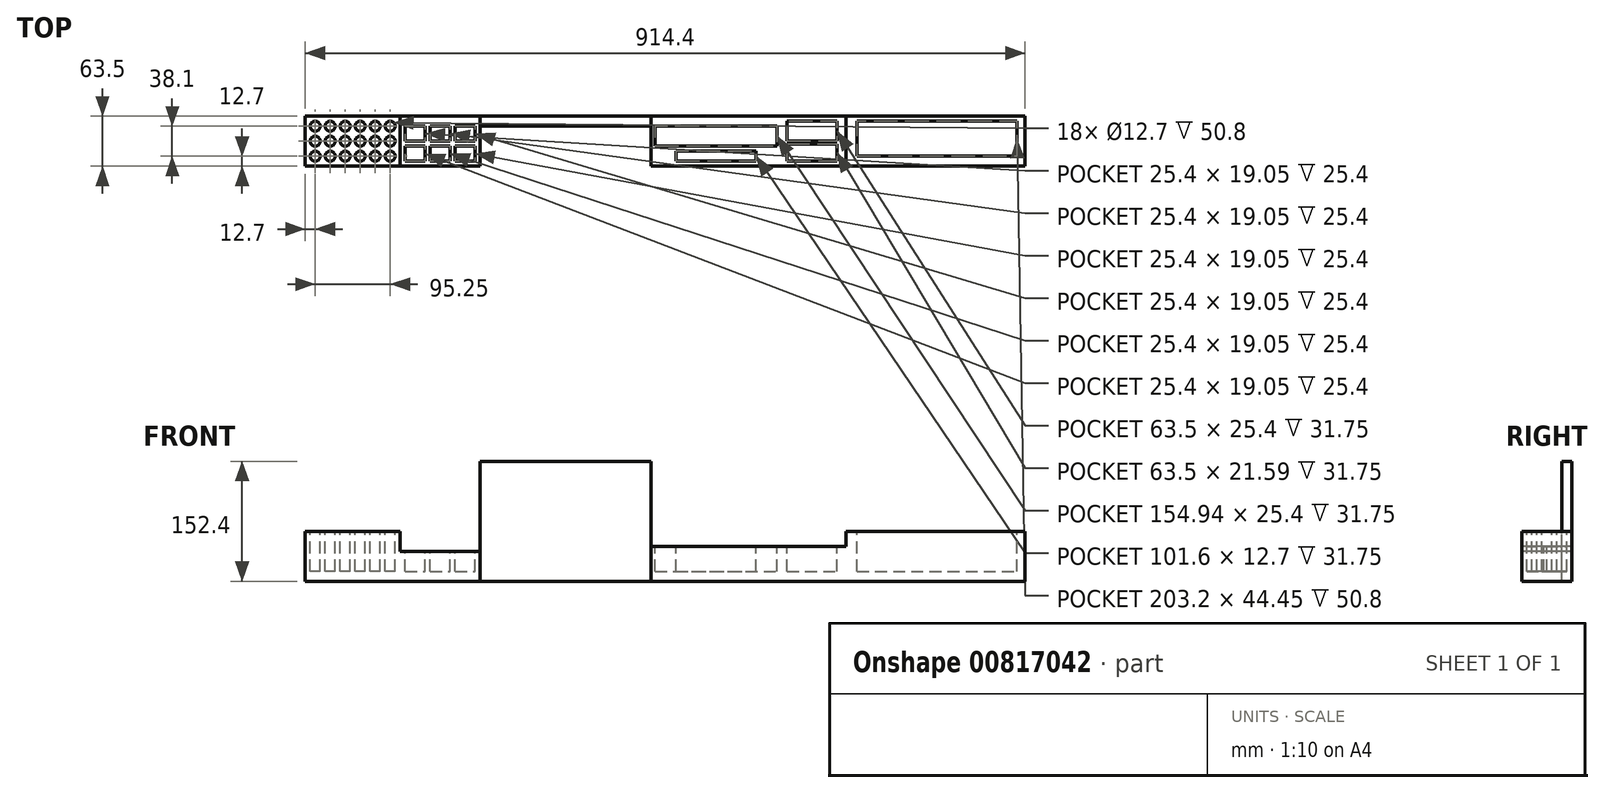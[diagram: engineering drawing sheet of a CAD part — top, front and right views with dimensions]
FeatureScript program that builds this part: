
annotation { "Feature Type Name" : "Feature", "Feature Type Description" : "" }
export const myFeature = defineFeature(function(context is Context, id is Id, definition is map)
    precondition{}
    {
        {
            var Q0;
            Q0=qCreatedBy(makeId("Front.planeOp"),FACE);
            var sketch = newSketch(context, id + "F0", { "sketchPlane" : qUnion([Q0])});
            skLineSegment(sketch, "E0.bottom", {"start": v(457.2, 76.2) * mm, "end": v(-457.2, 76.2) * mm});
            skLineSegment(sketch, "E0.top", {"start": v(457.2, -76.2) * mm, "end": v(-457.2, -76.2) * mm});
            skLineSegment(sketch, "E0.left", {"start": v(457.2, 76.2) * mm, "end": v(457.2, -76.2) * mm});
            skLineSegment(sketch, "E0.right", {"start": v(-457.2, 76.2) * mm, "end": v(-457.2, -76.2) * mm});
            skPoint(sketch, "E0.middle", {"position": v(0, 0) * mm});
            skSolve(sketch);
        }
        {
            var Q0;
            Q0=makeQuery(id+"F0.imprint","IMPRINT",FACE,{"disambiguationData":[TD([[makeQuery(id+"F0.imprint","IMPRINT",EDGE,{"derivedFrom":sQuery(id+"F0.wireOp",EDGE,"E0.bottom")}),1.0]])]});
            extrude(context, id + "F1", {"entities" : qUnion([Q0]), "depth" : 63.5 * mm, "offsetDistance" : 25.4 * mm});
        }
        {
            var Q0;
            Q0=makeQuery(id+"F1.opExtrude","SWEPT_FACE",FACE,{"disambiguationData":[OSD([sQuery(id+"F0.wireOp",EDGE,"E0.bottom")])]});
            var sketch = newSketch(context, id + "F2", { "sketchPlane" : qUnion([Q0])});
            skCircle(sketch, "E1", {"center": v(-444.5, -12.7) * mm, "radius": 6.35 * mm});
            skCircle(sketch, "E2", {"center": v(-425.45, -12.7) * mm, "radius": 6.35 * mm});
            skCircle(sketch, "E3", {"center": v(-406.4, -12.7) * mm, "radius": 6.35 * mm});
            skCircle(sketch, "E4", {"center": v(-387.35, -12.7) * mm, "radius": 6.35 * mm});
            skCircle(sketch, "E5", {"center": v(-368.3, -12.7) * mm, "radius": 6.35 * mm});
            skCircle(sketch, "E6", {"center": v(-349.25, -12.7) * mm, "radius": 6.35 * mm});
            skCircle(sketch, "E7", {"center": v(-444.5, -31.75) * mm, "radius": 6.35 * mm});
            skCircle(sketch, "E8", {"center": v(-425.45, -31.75) * mm, "radius": 6.35 * mm});
            skCircle(sketch, "E9", {"center": v(-406.4, -31.75) * mm, "radius": 6.35 * mm});
            skCircle(sketch, "E10", {"center": v(-387.35, -31.75) * mm, "radius": 6.35 * mm});
            skCircle(sketch, "E11", {"center": v(-368.3, -31.75) * mm, "radius": 6.35 * mm});
            skCircle(sketch, "E12", {"center": v(-349.25, -31.75) * mm, "radius": 6.35 * mm});
            skCircle(sketch, "E13", {"center": v(-444.5, -50.8) * mm, "radius": 6.35 * mm});
            skCircle(sketch, "E14", {"center": v(-425.45, -50.8) * mm, "radius": 6.35 * mm});
            skCircle(sketch, "E15", {"center": v(-406.4, -50.8) * mm, "radius": 6.35 * mm});
            skCircle(sketch, "E16", {"center": v(-387.35, -50.8) * mm, "radius": 6.35 * mm});
            skCircle(sketch, "E17", {"center": v(-368.3, -50.8) * mm, "radius": 6.35 * mm});
            skCircle(sketch, "E18", {"center": v(-349.25, -50.8) * mm, "radius": 6.35 * mm});
            skLineSegment(sketch, "E19.bottom", {"start": v(-330.2, -57.15) * mm, "end": v(-304.8, -57.15) * mm});
            skLineSegment(sketch, "E19.top", {"start": v(-330.2, -38.1) * mm, "end": v(-304.8, -38.1) * mm});
            skLineSegment(sketch, "E19.left", {"start": v(-330.2, -57.15) * mm, "end": v(-330.2, -38.1) * mm});
            skLineSegment(sketch, "E19.right", {"start": v(-304.8, -57.15) * mm, "end": v(-304.8, -38.1) * mm});
            skLineSegment(sketch, "E20.bottom", {"start": v(-330.2, -31.75) * mm, "end": v(-304.8, -31.75) * mm});
            skLineSegment(sketch, "E20.top", {"start": v(-330.2, -12.7) * mm, "end": v(-304.8, -12.7) * mm});
            skLineSegment(sketch, "E20.left", {"start": v(-330.2, -31.75) * mm, "end": v(-330.2, -12.7) * mm});
            skLineSegment(sketch, "E20.right", {"start": v(-304.8, -31.75) * mm, "end": v(-304.8, -12.7) * mm});
            skLineSegment(sketch, "E21.bottom", {"start": v(-298.45, -31.75) * mm, "end": v(-273.05, -31.75) * mm});
            skLineSegment(sketch, "E21.top", {"start": v(-298.45, -12.7) * mm, "end": v(-273.05, -12.7) * mm});
            skLineSegment(sketch, "E21.left", {"start": v(-298.45, -31.75) * mm, "end": v(-298.45, -12.7) * mm});
            skLineSegment(sketch, "E21.right", {"start": v(-273.05, -31.75) * mm, "end": v(-273.05, -12.7) * mm});
            skLineSegment(sketch, "E22.bottom", {"start": v(-298.45, -57.15) * mm, "end": v(-273.05, -57.15) * mm});
            skLineSegment(sketch, "E22.top", {"start": v(-298.45, -38.1) * mm, "end": v(-273.05, -38.1) * mm});
            skLineSegment(sketch, "E22.left", {"start": v(-298.45, -57.15) * mm, "end": v(-298.45, -38.1) * mm});
            skLineSegment(sketch, "E22.right", {"start": v(-273.05, -57.15) * mm, "end": v(-273.05, -38.1) * mm});
            skLineSegment(sketch, "E23.bottom", {"start": v(-266.7, -31.75) * mm, "end": v(-241.3, -31.75) * mm});
            skLineSegment(sketch, "E23.top", {"start": v(-266.7, -12.7) * mm, "end": v(-241.3, -12.7) * mm});
            skLineSegment(sketch, "E23.left", {"start": v(-266.7, -31.75) * mm, "end": v(-266.7, -12.7) * mm});
            skLineSegment(sketch, "E23.right", {"start": v(-241.3, -31.75) * mm, "end": v(-241.3, -12.7) * mm});
            skLineSegment(sketch, "E24.bottom", {"start": v(-266.7, -57.15) * mm, "end": v(-241.3, -57.15) * mm});
            skLineSegment(sketch, "E24.top", {"start": v(-266.7, -38.1) * mm, "end": v(-241.3, -38.1) * mm});
            skLineSegment(sketch, "E24.left", {"start": v(-266.7, -57.15) * mm, "end": v(-266.7, -38.1) * mm});
            skLineSegment(sketch, "E24.right", {"start": v(-241.3, -57.15) * mm, "end": v(-241.3, -38.1) * mm});
            skLineSegment(sketch, "E25", {"start": v(-228.6, 0) * mm, "end": v(-228.6, -63.5) * mm, "construction": true});
            skLineSegment(sketch, "E26", {"start": v(-25.4, 0) * mm, "end": v(-25.4, -63.5) * mm, "construction": true});
            skLineSegment(sketch, "E27.bottom", {"start": v(-12.7, -12.7) * mm, "end": v(142.24, -12.7) * mm});
            skLineSegment(sketch, "E27.top", {"start": v(-12.7, -38.1) * mm, "end": v(142.24, -38.1) * mm});
            skLineSegment(sketch, "E27.left", {"start": v(-12.7, -12.7) * mm, "end": v(-12.7, -38.1) * mm});
            skLineSegment(sketch, "E27.right", {"start": v(142.24, -12.7) * mm, "end": v(142.24, -38.1) * mm});
            skLineSegment(sketch, "E28.bottom", {"start": v(13.97, -44.45) * mm, "end": v(115.57, -44.45) * mm});
            skLineSegment(sketch, "E28.top", {"start": v(13.97, -57.15) * mm, "end": v(115.57, -57.15) * mm});
            skLineSegment(sketch, "E28.left", {"start": v(13.97, -44.45) * mm, "end": v(13.97, -57.15) * mm});
            skLineSegment(sketch, "E28.right", {"start": v(115.57, -44.45) * mm, "end": v(115.57, -57.15) * mm});
            skLineSegment(sketch, "E29.bottom", {"start": v(154.94, -6.35) * mm, "end": v(218.44, -6.35) * mm});
            skLineSegment(sketch, "E29.top", {"start": v(154.94, -31.75) * mm, "end": v(218.44, -31.75) * mm});
            skLineSegment(sketch, "E29.left", {"start": v(154.94, -6.35) * mm, "end": v(154.94, -31.75) * mm});
            skLineSegment(sketch, "E29.right", {"start": v(218.44, -6.35) * mm, "end": v(218.44, -31.75) * mm});
            skLineSegment(sketch, "E30.bottom", {"start": v(243.84, -6.35) * mm, "end": v(447.04, -6.35) * mm});
            skLineSegment(sketch, "E30.top", {"start": v(243.84, -50.8) * mm, "end": v(447.04, -50.8) * mm});
            skLineSegment(sketch, "E30.left", {"start": v(243.84, -6.35) * mm, "end": v(243.84, -50.8) * mm});
            skLineSegment(sketch, "E30.right", {"start": v(447.04, -6.35) * mm, "end": v(447.04, -50.8) * mm});
            skLineSegment(sketch, "E31.bottom", {"start": v(154.94, -57.15) * mm, "end": v(218.44, -57.15) * mm});
            skLineSegment(sketch, "E31.top", {"start": v(154.94, -35.56) * mm, "end": v(218.44, -35.56) * mm});
            skLineSegment(sketch, "E31.left", {"start": v(154.94, -57.15) * mm, "end": v(154.94, -35.56) * mm});
            skLineSegment(sketch, "E31.right", {"start": v(218.44, -57.15) * mm, "end": v(218.44, -35.56) * mm});
            skSolve(sketch);
        }
        {
            var Q0;
            Q0 = qSketchRegion(id + "F2", true);
            extrude(context, id + "F3", {"entities" : qUnion([Q0]), "operationType" : NewBodyOperationType.REMOVE, "oppositeDirection" : true, "depth" : 139.7 * mm, "offsetDistance" : 25.4 * mm});
        }
        {
            var Q0;
            Q0=makeQuery(id+"F1.opExtrude","SWEPT_FACE",FACE,{"disambiguationData":[OSD([sQuery(id+"F0.wireOp",EDGE,"E0.bottom")])]});
            var sketch = newSketch(context, id + "F4", { "sketchPlane" : qUnion([Q0])});
            skLineSegment(sketch, "E32.bottom", {"start": v(-457.2, 0) * mm, "end": v(-336.55, 0) * mm});
            skLineSegment(sketch, "E32.top", {"start": v(-457.2, -63.5) * mm, "end": v(-336.55, -63.5) * mm});
            skLineSegment(sketch, "E32.left", {"start": v(-457.2, 0) * mm, "end": v(-457.2, -63.5) * mm});
            skLineSegment(sketch, "E32.right", {"start": v(-336.55, 0) * mm, "end": v(-336.55, -63.5) * mm});
            skSolve(sketch);
        }
        {
            var Q0;
            Q0 = qSketchRegion(id + "F4", true);
            extrude(context, id + "F5", {"entities" : qUnion([Q0]), "operationType" : NewBodyOperationType.REMOVE, "oppositeDirection" : true, "depth" : 88.9 * mm, "offsetDistance" : 25.4 * mm});
        }
        {
            var Q0;
            Q0=makeQuery(id+"F1.opExtrude","SWEPT_FACE",FACE,{"disambiguationData":[OSD([sQuery(id+"F0.wireOp",EDGE,"E0.bottom")])]});
            var sketch = newSketch(context, id + "F6", { "sketchPlane" : qUnion([Q0])});
            skLineSegment(sketch, "E33.bottom", {"start": v(-336.55, 0) * mm, "end": v(-234.95, 0) * mm});
            skLineSegment(sketch, "E33.top", {"start": v(-336.55, -63.5) * mm, "end": v(-234.95, -63.5) * mm});
            skLineSegment(sketch, "E33.left", {"start": v(-336.55, 0) * mm, "end": v(-336.55, -63.5) * mm});
            skLineSegment(sketch, "E33.right", {"start": v(-234.95, 0) * mm, "end": v(-234.95, -63.5) * mm});
            skSolve(sketch);
        }
        {
            var Q0;
            Q0 = qSketchRegion(id + "F6", true);
            extrude(context, id + "F7", {"entities" : qUnion([Q0]), "operationType" : NewBodyOperationType.REMOVE, "oppositeDirection" : true, "depth" : 114.3 * mm, "offsetDistance" : 25.4 * mm});
        }
        {
            var Q0;
            Q0=makeQuery(id+"F1.opExtrude","SWEPT_FACE",FACE,{"disambiguationData":[OSD([sQuery(id+"F0.wireOp",EDGE,"E0.bottom")])]});
            var sketch = newSketch(context, id + "F8", { "sketchPlane" : qUnion([Q0])});
            skLineSegment(sketch, "E34.bottom", {"start": v(-17.78, 0) * mm, "end": v(229.87, 0) * mm});
            skLineSegment(sketch, "E34.top", {"start": v(-17.78, -63.5) * mm, "end": v(229.87, -63.5) * mm});
            skLineSegment(sketch, "E34.left", {"start": v(-17.78, 0) * mm, "end": v(-17.78, -63.5) * mm});
            skLineSegment(sketch, "E34.right", {"start": v(229.87, 0) * mm, "end": v(229.87, -63.5) * mm});
            skSolve(sketch);
        }
        {
            var Q0;
            Q0 = qSketchRegion(id + "F8", true);
            extrude(context, id + "F9", {"entities" : qUnion([Q0]), "operationType" : NewBodyOperationType.REMOVE, "oppositeDirection" : true, "depth" : 107.95 * mm, "offsetDistance" : 25.4 * mm});
        }
        {
            var Q0;
            {var subQ0=sQuery(id+"F0.wireOp",EDGE,"E0.left");var subQ3=sQuery(id+"F0.wireOp",EDGE,"E0.bottom");Q0=makeQuery(id+"F9.boolean.opBoolean","SPLIT",FACE,{"disambiguationData":[TD([makeQuery(id+"F1.opExtrude","SWEPT_FACE",FACE,{"disambiguationData":[OSD([subQ0])]})])],"derivedFrom":makeQuery(id+"F1.opExtrude","SWEPT_FACE",FACE,{"disambiguationData":[OSD([subQ3])]})});}
            var sketch = newSketch(context, id + "F10", { "sketchPlane" : qUnion([Q0])});
            skLineSegment(sketch, "E35.bottom", {"start": v(229.87, -63.5) * mm, "end": v(457.2, -63.5) * mm});
            skLineSegment(sketch, "E35.top", {"start": v(229.87, 0) * mm, "end": v(457.2, 0) * mm});
            skLineSegment(sketch, "E35.left", {"start": v(229.87, -63.5) * mm, "end": v(229.87, 0) * mm});
            skLineSegment(sketch, "E35.right", {"start": v(457.2, -63.5) * mm, "end": v(457.2, 0) * mm});
            skSolve(sketch);
        }
        {
            var Q0;
            Q0 = qSketchRegion(id + "F10", true);
            extrude(context, id + "F11", {"entities" : qUnion([Q0]), "operationType" : NewBodyOperationType.REMOVE, "oppositeDirection" : true, "depth" : 88.9 * mm, "offsetDistance" : 25.4 * mm});
        }
        {
            var Q0;
            {var subQ3=sQuery(id+"F0.wireOp",EDGE,"E0.bottom");Q0=makeQuery(id+"F9.boolean.opBoolean","SPLIT",FACE,{"disambiguationData":[TD([makeQuery(id+"F7.boolean.opBoolean","COPY",FACE,{"derivedFrom":makeQuery(id+"F7.opExtrude","SWEPT_FACE",FACE,{"disambiguationData":[OSD([sQuery(id+"F6.wireOp",EDGE,"E33.right")])]})})])],"derivedFrom":makeQuery(id+"F1.opExtrude","SWEPT_FACE",FACE,{"disambiguationData":[OSD([subQ3])]})});}
            var sketch = newSketch(context, id + "F12", { "sketchPlane" : qUnion([Q0])});
            skLineSegment(sketch, "E36.bottom", {"start": v(-234.95, -63.5) * mm, "end": v(-17.78, -63.5) * mm});
            skLineSegment(sketch, "E36.top", {"start": v(-234.95, -12.7) * mm, "end": v(-17.78, -12.7) * mm});
            skLineSegment(sketch, "E36.left", {"start": v(-234.95, -63.5) * mm, "end": v(-234.95, -12.7) * mm});
            skLineSegment(sketch, "E36.right", {"start": v(-17.78, -63.5) * mm, "end": v(-17.78, -12.7) * mm});
            skSolve(sketch);
        }
        {
            var Q0;
            Q0 = qSketchRegion(id + "F12", true);
            extrude(context, id + "F13", {"entities" : qUnion([Q0]), "operationType" : NewBodyOperationType.REMOVE, "oppositeDirection" : true, "depth" : 152.4 * mm, "offsetDistance" : 25.4 * mm});
        }
    });
